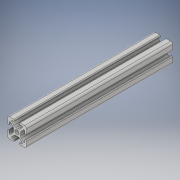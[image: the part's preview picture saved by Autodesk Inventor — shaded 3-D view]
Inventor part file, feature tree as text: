
AUTODESK INVENTOR PART (.ipt)
format: ipt  version: 2019 (Build 230136000, 136)  size: 200,704 bytes
history: native  units: mm
features: extrude x1, sketch x1, other x1
ambient origin geometry x8: Origin, YZ Plane, XZ Plane, XY Plane, X Axis, Y Axis, Z Axis, Center Point
bodies: Solid1 (feature_tree)
feature tree (3):
  extrude  "Extrusion1"  Depth=152.4mm TaperAngle=0.0deg
  sketch  "Sketch1"  dims[d0=152.4mm d1=20.0mm d2=0.0mm]
  other  "Boss-Extrude1"
